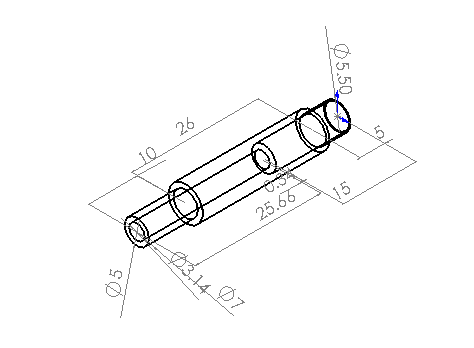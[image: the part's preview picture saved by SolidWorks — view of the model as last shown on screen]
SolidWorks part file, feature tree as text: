
SOLIDWORKS PART (.sldprt)
format: sldprt  version: not decoded by parser v0  size: 169,984 bytes
history: native  units: mm
features: sketch x5, cut_extrude x4, extrude x1 + 1 further entry (+10 scaffold rows collapsed)
feature tree (21):
  "Annotations"  RD1=3.14mm RD2=7mm RD3=10mm RD4=26mm RD5=5mm RD6=15mm RD7=25.66mm RD8=0.34mm RD9=5mm RD10=5.5mm
  scaffold x10  (default folders/planes/origin — collapsed)
  sketch  "Sketch1"  dims[D1=7.0mm]
  extrude  "Extrude1"  Depth=41mm
  sketch  "Sketch2"  dims[D1=1.5875mm]
  cut_extrude  "Cut-Extrude1"  Depth=25.66mm
  sketch  "Sketch3"  dims[D1=3.175mm]
  cut_extrude  "Cut-Extrude2"  Depth=15mm
  sketch  "Sketch4"  dims[D1=2.8mm]
  cut_extrude  "Cut-Extrude3"  Depth=5mm
  sketch  "Sketch5"
  cut_extrude  "Cut-Extrude4"  Depth=10mm
decode coverage: 9 of 10 modeling features carry decoded parameters; 1 rows unclassified (native names shown)
note: suppression state not decoded; provenance and decode notes live in map.json
